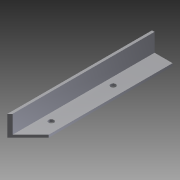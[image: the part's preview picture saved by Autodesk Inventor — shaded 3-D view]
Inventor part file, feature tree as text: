
AUTODESK INVENTOR PART (.ipt)
format: ipt  version: 2012 (Build 160160000, 160)  size: 89,600 bytes
history: native  units: in
note: dims shown in document units (in); Inventor stores cm internally (conversion verified against a paired STEP export)
features: extrude x2, sketch x2
ambient origin geometry x8: Origin, YZ Plane, XZ Plane, XY Plane, X Axis, Y Axis, Z Axis, Center Point
bodies: Solid1 (feature_tree)
feature tree (4):
  extrude  "Extrusion1"  Depth=1.0in
  extrude  "Extrusion2"  Depth=0.125in
  sketch  "Sketch1"  dims[d0=1.0in d1=1.0in]
  sketch  "Sketch2"  dims[d2=0.125in d3=0.125in d4=7.0in d5=0.0in d6=45.0deg d7=1.625in d8=3.0in d9=0.25in d10=0.5in d11=7.0in d12=0.0in]
